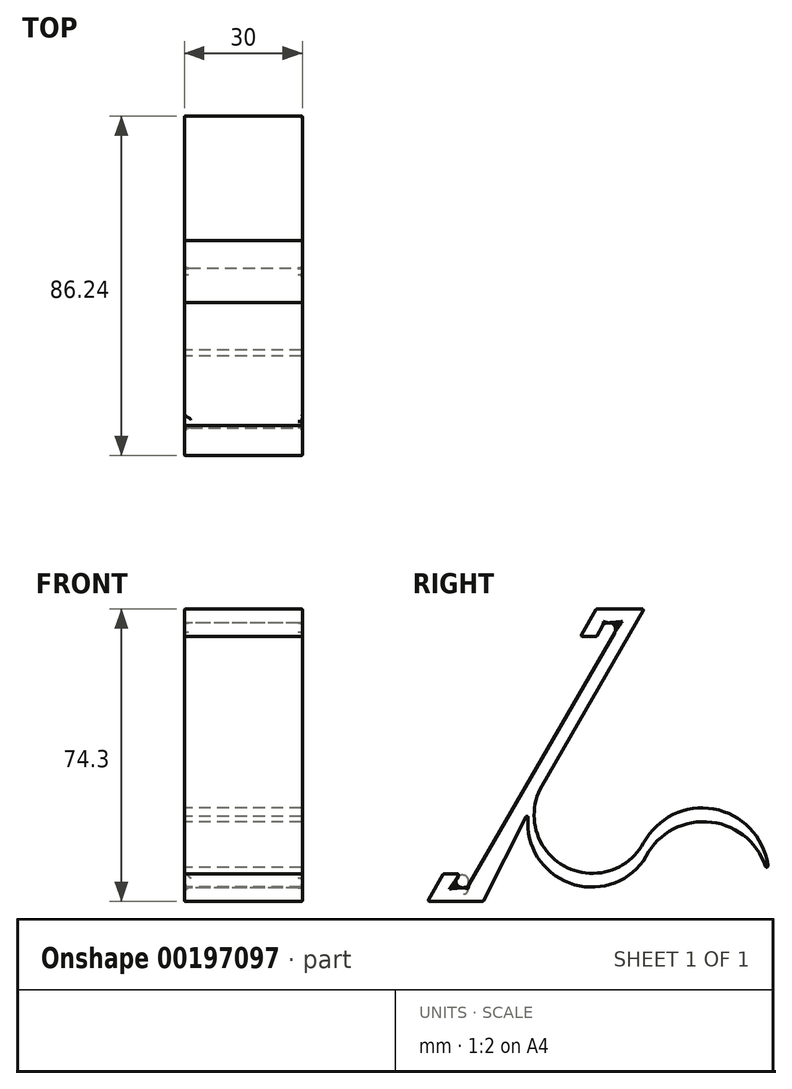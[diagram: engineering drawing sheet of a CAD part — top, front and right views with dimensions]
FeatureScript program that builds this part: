
annotation { "Feature Type Name" : "Feature", "Feature Type Description" : "" }
export const myFeature = defineFeature(function(context is Context, id is Id, definition is map)
    precondition{}
    {
        {
            var Q0;
            Q0=qCreatedBy(makeId("Right.planeOp"),FACE);
            var sketch = newSketch(context, id + "F0", { "sketchPlane" : qUnion([Q0])});
            skLineSegment(sketch, "E0", {"start": v(-25.84, 29.34) * mm, "end": v(0.12, 74.3) * mm});
            skLineSegment(sketch, "E1", {"start": v(0.12, 74.3) * mm, "end": v(-12, 74.3) * mm});
            skLineSegment(sketch, "E2", {"start": v(-12, 74.3) * mm, "end": v(-16.05, 67.3) * mm});
            skLineSegment(sketch, "E3", {"start": v(-16.05, 67.3) * mm, "end": v(-12, 67.3) * mm});
            skLineSegment(sketch, "E4", {"start": v(-12, 67.3) * mm, "end": v(-9.98, 70.8) * mm});
            skLineSegment(sketch, "E5", {"start": v(-9.98, 70.8) * mm, "end": v(-5.94, 70.8) * mm});
            skLineSegment(sketch, "E6", {"start": v(-5.94, 70.8) * mm, "end": v(-44.8, 3.5) * mm});
            skLineSegment(sketch, "E7", {"start": v(-44.8, 3.5) * mm, "end": v(-48.84, 3.5) * mm});
            skLineSegment(sketch, "E8", {"start": v(-48.84, 3.5) * mm, "end": v(-46.82, 7) * mm});
            skLineSegment(sketch, "E9", {"start": v(-46.82, 7) * mm, "end": v(-50.86, 7) * mm});
            skLineSegment(sketch, "E10", {"start": v(-50.86, 7) * mm, "end": v(-54.9, 0) * mm});
            skLineSegment(sketch, "E11", {"start": v(-54.9, 0) * mm, "end": v(-46.82, 0) * mm});
            skPoint(sketch, "E12", {"position": v(0.12, 74.3) * mm});
            skArc(sketch, "E13", {"start": v(-25.84, 29.34) * mm, "mid": v(-20.24, 9.02) * mm, "end": v(0, 14.9) * mm});
            skArc(sketch, "E14", {"start": v(0, 14.9) * mm, "mid": v(17.8, 23.48) * mm, "end": v(31.54, 9.3) * mm});
            skLineSegment(sketch, "E15", {"start": v(-40.78, 0) * mm, "end": v(-46.82, 0) * mm});
            skPoint(sketch, "E16", {"position": v(-29.1, 23.12) * mm});
            skPoint(sketch, "E17", {"position": v(0, 10.32) * mm});
            skPoint(sketch, "E18", {"position": v(31.75, 5.2) * mm});
            skArc(sketch, "E19", {"start": v(-29.1, 23.12) * mm, "mid": v(-19.7, 5.02) * mm, "end": v(0, 10.32) * mm});
            skArc(sketch, "E20", {"start": v(31.75, 5.2) * mm, "mid": v(17.86, 20.05) * mm, "end": v(0, 10.32) * mm});
            skLineSegment(sketch, "E21", {"start": v(-29.1, 23.12) * mm, "end": v(-40.78, 0) * mm});
            skLineSegment(sketch, "E22", {"start": v(31.54, 9.3) * mm, "end": v(31.75, 5.2) * mm});
            skSolve(sketch);
        }
        {
            var Q0;
            Q0=makeQuery(id+"F0.imprint","IMPRINT",FACE,{"disambiguationData":[TD([[makeQuery(id+"F0.imprint","IMPRINT",EDGE,{"derivedFrom":sQuery(id+"F0.wireOp",EDGE,"E0")}),1.0]])]});
            extrude(context, id + "F1", {"entities" : qUnion([Q0]), "depth" : 30 * mm});
        }
        {
            var Q0;
            Q0=makeQuery(id+"F1.opExtrude","SWEPT_FACE",FACE,{"disambiguationData":[OSD([sQuery(id+"F0.wireOp",EDGE,"E0")])]});
            var Q1;
            Q1=makeQuery(id+"F1.opExtrude","SWEPT_FACE",FACE,{"disambiguationData":[OSD([sQuery(id+"F0.wireOp",EDGE,"E13")])]});
            var Q2;
            Q2=makeQuery(id+"F1.opExtrude","SWEPT_FACE",FACE,{"disambiguationData":[OSD([sQuery(id+"F0.wireOp",EDGE,"E22")])]});
            var Q3;
            Q3=makeQuery(id+"F1.opExtrude","SWEPT_FACE",FACE,{"disambiguationData":[OSD([sQuery(id+"F0.wireOp",EDGE,"E1")])]});
            var Q4;
            Q4=makeQuery(id+"F1.opExtrude","SWEPT_FACE",FACE,{"disambiguationData":[OSD([sQuery(id+"F0.wireOp",EDGE,"E2")])]});
            var Q5;
            Q5=makeQuery(id+"F1.opExtrude","SWEPT_EDGE",EDGE,{"disambiguationData":[OSD([sQuery(id+"F0.wireOp",EDGE,"E3"),sQuery(id+"F0.wireOp",EDGE,"E4")])]});
            var Q6;
            Q6=makeQuery(id+"F1.opExtrude","CAP_EDGE",EDGE,{"disambiguationData":[OSD([sQuery(id+"F0.wireOp",EDGE,"E6")])],"isStart":true});
            var Q7;
            Q7=makeQuery(id+"F1.opExtrude","CAP_EDGE",EDGE,{"disambiguationData":[OSD([sQuery(id+"F0.wireOp",EDGE,"E6")])],"isStart":false});
            var Q8;
            Q8=makeQuery(id+"F1.opExtrude","SWEPT_FACE",FACE,{"disambiguationData":[OSD([sQuery(id+"F0.wireOp",EDGE,"E9")])]});
            var Q9;
            Q9=makeQuery(id+"F1.opExtrude","SWEPT_FACE",FACE,{"disambiguationData":[OSD([sQuery(id+"F0.wireOp",EDGE,"E10")])]});
            fillet(context, id + "F2", {"entities" : qUnion([Q0, Q1, Q2, Q3, Q4, Q5, Q6, Q7, Q8, Q9]), "radius" : 0.3 * mm, "tangentPropagation" : true, "allowEdgeOverflow" : false});
        }
        {
            var Q0;
            Q0=makeQuery(id+"F1.opExtrude","SWEPT_FACE",FACE,{"disambiguationData":[OSD([sQuery(id+"F0.wireOp",EDGE,"E20")])]});
            var Q1;
            Q1=makeQuery(id+"F1.opExtrude","SWEPT_FACE",FACE,{"disambiguationData":[OSD([sQuery(id+"F0.wireOp",EDGE,"E19")])]});
            var Q2;
            Q2=makeQuery(id+"F1.opExtrude","SWEPT_FACE",FACE,{"disambiguationData":[OSD([sQuery(id+"F0.wireOp",EDGE,"E11"),sQuery(id+"F0.wireOp",EDGE,"E15")])]});
            var Q3;
            Q3=makeQuery(id+"F1.opExtrude","CAP_FACE",FACE,{"disambiguationData":[OSD([sQuery(id+"F0.wireOp",EDGE,"E0"),sQuery(id+"F0.wireOp",EDGE,"E1"),sQuery(id+"F0.wireOp",EDGE,"E2"),sQuery(id+"F0.wireOp",EDGE,"E3"),sQuery(id+"F0.wireOp",EDGE,"E4"),sQuery(id+"F0.wireOp",EDGE,"E5"),sQuery(id+"F0.wireOp",EDGE,"E6"),sQuery(id+"F0.wireOp",EDGE,"E7"),sQuery(id+"F0.wireOp",EDGE,"E8"),sQuery(id+"F0.wireOp",EDGE,"E9"),sQuery(id+"F0.wireOp",EDGE,"E10"),sQuery(id+"F0.wireOp",EDGE,"E11"),sQuery(id+"F0.wireOp",EDGE,"E13"),sQuery(id+"F0.wireOp",EDGE,"E14"),sQuery(id+"F0.wireOp",EDGE,"E15"),sQuery(id+"F0.wireOp",EDGE,"E19"),sQuery(id+"F0.wireOp",EDGE,"E20"),sQuery(id+"F0.wireOp",EDGE,"E21"),sQuery(id+"F0.wireOp",EDGE,"E22")])],"isStart":false});
            var Q4;
            Q4=makeQuery(id+"F1.opExtrude","SWEPT_FACE",FACE,{"disambiguationData":[OSD([sQuery(id+"F0.wireOp",EDGE,"E3")])]});
            var Q5;
            Q5=makeQuery(id+"F1.opExtrude","CAP_EDGE",EDGE,{"disambiguationData":[OSD([sQuery(id+"F0.wireOp",EDGE,"E5")])],"isStart":true});
            var Q6;
            Q6=makeQuery(id+"F1.opExtrude","SWEPT_EDGE",EDGE,{"disambiguationData":[OSD([sQuery(id+"F0.wireOp",EDGE,"E19"),sQuery(id+"F0.wireOp",EDGE,"E20")])]});
            fillet(context, id + "F3", {"entities" : qUnion([Q0, Q1, Q2, Q3, Q4, Q5, Q6]), "radius" : 0.3 * mm, "tangentPropagation" : true, "allowEdgeOverflow" : false});
        }
        {
            var Q0;
            Q0=makeQuery(id+"F1.opExtrude","SWEPT_EDGE",EDGE,{"disambiguationData":[OSD([sQuery(id+"F0.wireOp",EDGE,"E5"),sQuery(id+"F0.wireOp",EDGE,"E6")])]});
            var Q1;
            Q1=makeQuery(id+"F1.opExtrude","SWEPT_EDGE",EDGE,{"disambiguationData":[OSD([sQuery(id+"F0.wireOp",EDGE,"E4"),sQuery(id+"F0.wireOp",EDGE,"E5")])]});
            var Q2;
            Q2=makeQuery(id+"F1.opExtrude","SWEPT_FACE",FACE,{"disambiguationData":[OSD([sQuery(id+"F0.wireOp",EDGE,"E7")])]});
            var Q3;
            Q3=makeQuery(id+"F1.opExtrude","SWEPT_FACE",FACE,{"disambiguationData":[OSD([sQuery(id+"F0.wireOp",EDGE,"E5")])]});
            fillet(context, id + "F4", {"entities" : qUnion([Q0, Q1, Q2, Q3]), "radius" : 1.6 * mm, "tangentPropagation" : true, "allowEdgeOverflow" : false});
        }
    });
